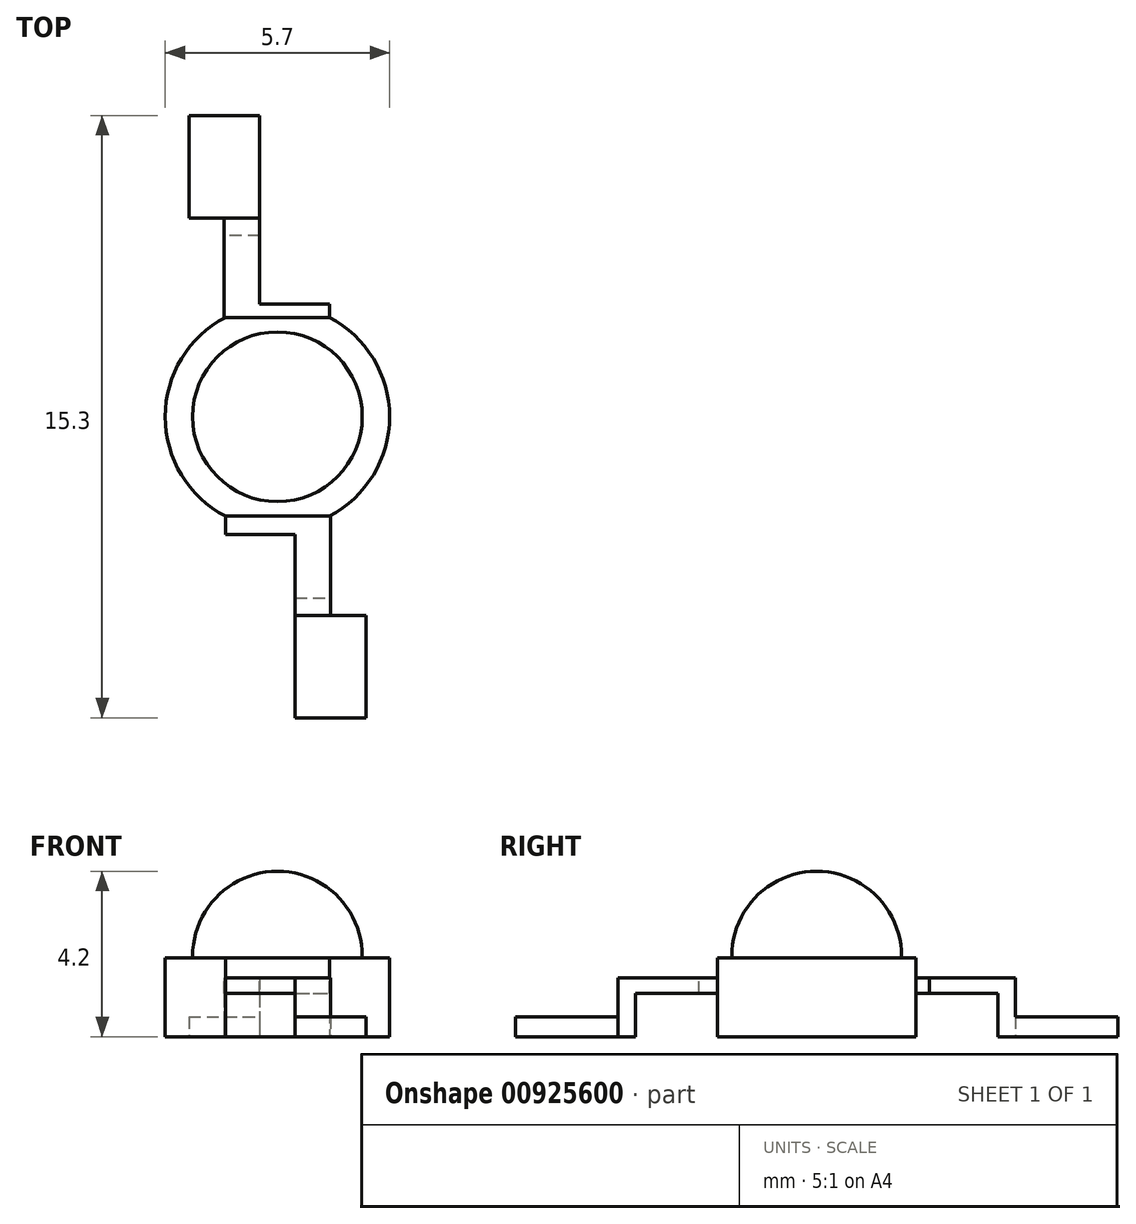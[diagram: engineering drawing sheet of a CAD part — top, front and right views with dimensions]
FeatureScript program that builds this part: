
annotation { "Feature Type Name" : "Feature", "Feature Type Description" : "" }
export const myFeature = defineFeature(function(context is Context, id is Id, definition is map)
    precondition{}
    {
        {
            var Q0;
            Q0=qCreatedBy(makeId("Top.planeOp"),FACE);
            var sketch = newSketch(context, id + "F0", { "sketchPlane" : qUnion([Q0])});
            skPoint(sketch, "E0.0", {"position": v(0, -4.6) * mm});
            skPoint(sketch, "E1.0", {"position": v(2.7, -4.6) * mm});
            skPoint(sketch, "E2.0", {"position": v(2.7, -8.1) * mm});
            skPoint(sketch, "E3.0", {"position": v(0, -8.1) * mm});
            skPoint(sketch, "E4.0", {"position": v(-2.7, 4.6) * mm});
            skPoint(sketch, "E5.0", {"position": v(0, 4.6) * mm});
            skPoint(sketch, "E6.0", {"position": v(-2.7, 8.1) * mm});
            skPoint(sketch, "E7.0", {"position": v(0, 8.1) * mm});
            skPoint(sketch, "E8.0", {"position": v(0, 2.85) * mm});
            skPoint(sketch, "E9.0", {"position": v(0, -2.85) * mm});
            skPoint(sketch, "E10.0", {"position": v(2.85, 0) * mm});
            skPoint(sketch, "E11.0", {"position": v(-2.85, 0) * mm});
            skLineSegment(sketch, "E12.bottom", {"start": v(-2.7, 8.1) * mm, "end": v(0, 8.1) * mm, "construction": true});
            skLineSegment(sketch, "E12.top", {"start": v(-2.7, 4.6) * mm, "end": v(0, 4.6) * mm, "construction": true});
            skLineSegment(sketch, "E12.left", {"start": v(-2.7, 8.1) * mm, "end": v(-2.7, 4.6) * mm, "construction": true});
            skLineSegment(sketch, "E12.right", {"start": v(0, 8.1) * mm, "end": v(0, 4.6) * mm, "construction": true});
            skLineSegment(sketch, "E13.bottom", {"start": v(0, -8.1) * mm, "end": v(2.7, -8.1) * mm, "construction": true});
            skLineSegment(sketch, "E13.top", {"start": v(0, -4.6) * mm, "end": v(2.7, -4.6) * mm, "construction": true});
            skLineSegment(sketch, "E13.left", {"start": v(0, -8.1) * mm, "end": v(0, -4.6) * mm, "construction": true});
            skLineSegment(sketch, "E13.right", {"start": v(2.7, -8.1) * mm, "end": v(2.7, -4.6) * mm, "construction": true});
            skArc(sketch, "E14", {"start": v(-1.32, 2.53) * mm, "mid": v(-2.85, 0) * mm, "end": v(-1.32, -2.53) * mm});
            skLineSegment(sketch, "E15.0", {"start": v(-2.25, 5.05) * mm, "end": v(-0.45, 5.05) * mm});
            skLineSegment(sketch, "E15.1", {"start": v(-2.25, 7.65) * mm, "end": v(-2.25, 5.05) * mm});
            skLineSegment(sketch, "E15.2", {"start": v(-2.25, 7.65) * mm, "end": v(-0.45, 7.65) * mm});
            skLineSegment(sketch, "E15.3", {"start": v(-0.45, 7.65) * mm, "end": v(-0.45, 5.05) * mm});
            skLineSegment(sketch, "E16.0", {"start": v(0.45, -7.65) * mm, "end": v(2.25, -7.65) * mm});
            skLineSegment(sketch, "E16.1", {"start": v(0.45, -7.65) * mm, "end": v(0.45, -5.05) * mm});
            skLineSegment(sketch, "E16.2", {"start": v(0.45, -5.05) * mm, "end": v(2.25, -5.05) * mm});
            skLineSegment(sketch, "E16.3", {"start": v(2.25, -7.65) * mm, "end": v(2.25, -5.05) * mm});
            skLineSegment(sketch, "E17.bottom", {"start": v(-1.32, 2.53) * mm, "end": v(1.32, 2.53) * mm});
            skLineSegment(sketch, "E17.top", {"start": v(-1.32, -2.53) * mm, "end": v(1.32, -2.53) * mm});
            skLineSegment(sketch, "E18", {"start": v(0, -0.92) * mm, "end": v(0, 1.01) * mm, "construction": true});
            skArc(sketch, "E19.trimOffspring", {"start": v(1.32, -2.53) * mm, "mid": v(2.85, 0) * mm, "end": v(1.32, 2.53) * mm});
            skSolve(sketch);
        }
        {
            var Q0;
            Q0=makeQuery(id+"F0.imprint","IMPRINT",FACE,{"disambiguationData":[TD([[makeQuery(id+"F0.imprint","IMPRINT",EDGE,{"derivedFrom":sQuery(id+"F0.wireOp",EDGE,"E15.0")}),1.0]])]});
            var Q1;
            Q1=makeQuery(id+"F0.imprint","IMPRINT",FACE,{"disambiguationData":[TD([[makeQuery(id+"F0.imprint","IMPRINT",EDGE,{"derivedFrom":sQuery(id+"F0.wireOp",EDGE,"E16.0")}),1.0]])]});
            var Q2;
            Q2=sQuery(id+"F0.wireOp",EDGE,"E16.1");
            var Q3;
            Q3=sQuery(id+"F0.wireOp",EDGE,"E16.2");
            var Q4;
            Q4=sQuery(id+"F0.wireOp",EDGE,"E16.3");
            var Q5;
            Q5=sQuery(id+"F0.wireOp",EDGE,"E16.0");
            var Q6;
            Q6=sQuery(id+"F0.wireOp",EDGE,"E15.2");
            extrude(context, id + "F1", {"entities" : qUnion([Q0, Q1]), "surfaceEntities" : qUnion([Q2, Q3, Q4, Q5, Q6]), "depth" : .5 * mm, "offsetDistance" : 25 * mm});
        }
        {
            var Q0;
            Q0=makeQuery(id+"F0.imprint","IMPRINT",FACE,{"disambiguationData":[TD([[makeQuery(id+"F0.imprint","IMPRINT",EDGE,{"derivedFrom":sQuery(id+"F0.wireOp",EDGE,"E14")}),1.0]])]});
            extrude(context, id + "F2", {"entities" : qUnion([Q0]), "depth" : 2 * mm, "offsetDistance" : 25 * mm});
        }
        {
            var Q0;
            Q0=makeQuery(id+"F1.opExtrude","CAP_FACE",FACE,{"disambiguationData":[OSD([sQuery(id+"F0.wireOp",EDGE,"E16.0"),sQuery(id+"F0.wireOp",EDGE,"E16.1"),sQuery(id+"F0.wireOp",EDGE,"E16.2"),sQuery(id+"F0.wireOp",EDGE,"E16.3")])],"isStart":false});
            var sketch = newSketch(context, id + "F3", { "sketchPlane" : qUnion([Q0])});
            skPoint(sketch, "E20.oppositeSnap0", {"position": v(1.35, -5.05) * mm});
            skLineSegment(sketch, "E20.bottom", {"start": v(0.45, -5.05) * mm, "end": v(1.35, -5.05) * mm});
            skLineSegment(sketch, "E20.top", {"start": v(0.45, -4.6) * mm, "end": v(1.35, -4.6) * mm});
            skLineSegment(sketch, "E20.left", {"start": v(0.45, -5.05) * mm, "end": v(0.45, -4.6) * mm});
            skLineSegment(sketch, "E20.right", {"start": v(1.35, -5.05) * mm, "end": v(1.35, -4.6) * mm});
            skPoint(sketch, "E21.0", {"position": v(-0.45, 5.05) * mm});
            skPoint(sketch, "E22.0", {"position": v(-1.35, 5.05) * mm});
            skLineSegment(sketch, "E23.bottom", {"start": v(-0.45, 5.05) * mm, "end": v(-1.35, 5.05) * mm});
            skLineSegment(sketch, "E23.top", {"start": v(-0.45, 4.6) * mm, "end": v(-1.35, 4.6) * mm});
            skLineSegment(sketch, "E23.left", {"start": v(-0.45, 5.05) * mm, "end": v(-0.45, 4.6) * mm});
            skLineSegment(sketch, "E23.right", {"start": v(-1.35, 5.05) * mm, "end": v(-1.35, 4.6) * mm});
            skSolve(sketch);
        }
        {
            var Q0;
            Q0 = qSketchRegion(id + "F3", true);
            extrude(context, id + "F4", {"entities" : qUnion([Q0]), "operationType" : NewBodyOperationType.ADD, "depth" : 1 * mm, "offsetDistance" : 25 * mm, "hasSecondDirection" : true, "secondDirectionOppositeDirection" : true, "secondDirectionDepth" : .5 * mm});
        }
        {
            var Q0;
            Q0=makeQuery(id+"F4.opExtrude","CAP_FACE",FACE,{"disambiguationData":[OSD([sQuery(id+"F3.wireOp",EDGE,"E20.bottom"),sQuery(id+"F3.wireOp",EDGE,"E20.top"),sQuery(id+"F3.wireOp",EDGE,"E20.left"),sQuery(id+"F3.wireOp",EDGE,"E20.right")])],"isStart":false});
            var sketch = newSketch(context, id + "F5", { "sketchPlane" : qUnion([Q0])});
            skLineSegment(sketch, "E24.bottom", {"start": v(1.35, -4.6) * mm, "end": v(0.45, -4.6) * mm});
            skLineSegment(sketch, "E24.top", {"start": v(1.35, -2.53) * mm, "end": v(0.45, -2.53) * mm});
            skLineSegment(sketch, "E24.left", {"start": v(1.35, -4.6) * mm, "end": v(1.35, -2.53) * mm});
            skLineSegment(sketch, "E24.right", {"start": v(0.45, -4.6) * mm, "end": v(0.45, -2.99) * mm});
            skLineSegment(sketch, "E25.0", {"start": v(-1.32, -2.53) * mm, "end": v(1.32, -2.53) * mm, "construction": true});
            skLineSegment(sketch, "E26.0", {"start": v(-0.45, 4.6) * mm, "end": v(-1.35, 4.6) * mm, "construction": true});
            skLineSegment(sketch, "E27.0", {"start": v(-1.32, 2.53) * mm, "end": v(1.32, 2.53) * mm, "construction": true});
            skLineSegment(sketch, "E28.bottom", {"start": v(-1.35, 4.6) * mm, "end": v(-0.45, 4.6) * mm});
            skLineSegment(sketch, "E28.top", {"start": v(-1.35, 2.53) * mm, "end": v(-0.45, 2.53) * mm});
            skLineSegment(sketch, "E28.left", {"start": v(-1.35, 4.6) * mm, "end": v(-1.35, 2.53) * mm});
            skLineSegment(sketch, "E28.right", {"start": v(-0.45, 4.6) * mm, "end": v(-0.45, 2.87) * mm});
            skLineSegment(sketch, "E29.bottom", {"start": v(-0.45, 2.87) * mm, "end": v(1.32, 2.87) * mm});
            skLineSegment(sketch, "E29.top", {"start": v(-0.45, 2.53) * mm, "end": v(1.32, 2.53) * mm});
            skLineSegment(sketch, "E29.right", {"start": v(1.32, 2.87) * mm, "end": v(1.32, 2.53) * mm});
            skLineSegment(sketch, "E30.bottom", {"start": v(0.45, -2.99) * mm, "end": v(-1.32, -2.99) * mm});
            skLineSegment(sketch, "E30.top", {"start": v(0.45, -2.53) * mm, "end": v(-1.32, -2.53) * mm});
            skLineSegment(sketch, "E30.right", {"start": v(-1.32, -2.99) * mm, "end": v(-1.32, -2.53) * mm});
            skSolve(sketch);
        }
        {
            var Q0;
            Q0 = qSketchRegion(id + "F5", true);
            extrude(context, id + "F6", {"entities" : qUnion([Q0]), "operationType" : NewBodyOperationType.ADD, "oppositeDirection" : true, "depth" : .4 * mm, "offsetDistance" : 25 * mm});
        }
        {
            var Q0;
            Q0=makeQuery(id+"F2.opExtrude","CAP_FACE",FACE,{"disambiguationData":[OSD([sQuery(id+"F0.wireOp",EDGE,"E14"),sQuery(id+"F0.wireOp",EDGE,"E17.bottom"),sQuery(id+"F0.wireOp",EDGE,"E17.top"),sQuery(id+"F0.wireOp",EDGE,"E19.trimOffspring")])],"isStart":false});
            var sketch = newSketch(context, id + "F7", { "sketchPlane" : qUnion([Q0])});
            skCircle(sketch, "E31", {"center": v(0, 0) * mm, "radius": 2.16 * mm});
            skSolve(sketch);
        }
        {
            var Q0;
            Q0 = qSketchRegion(id + "F7", true);
            extrude(context, id + "F8", {"entities" : qUnion([Q0]), "depth" : 2.2 * mm, "offsetDistance" : 25 * mm});
        }
        {
            var Q0;
            Q0=makeQuery(id+"F8.opExtrude","CAP_EDGE",EDGE,{"disambiguationData":[OSD([sQuery(id+"F7.wireOp",EDGE,"E31")])],"isStart":false});
            fillet(context, id + "F9", {"entities" : qUnion([Q0]), "radius" : 2.15 * mm, "tangentPropagation" : true, "allowEdgeOverflow" : false});
        }
    });
